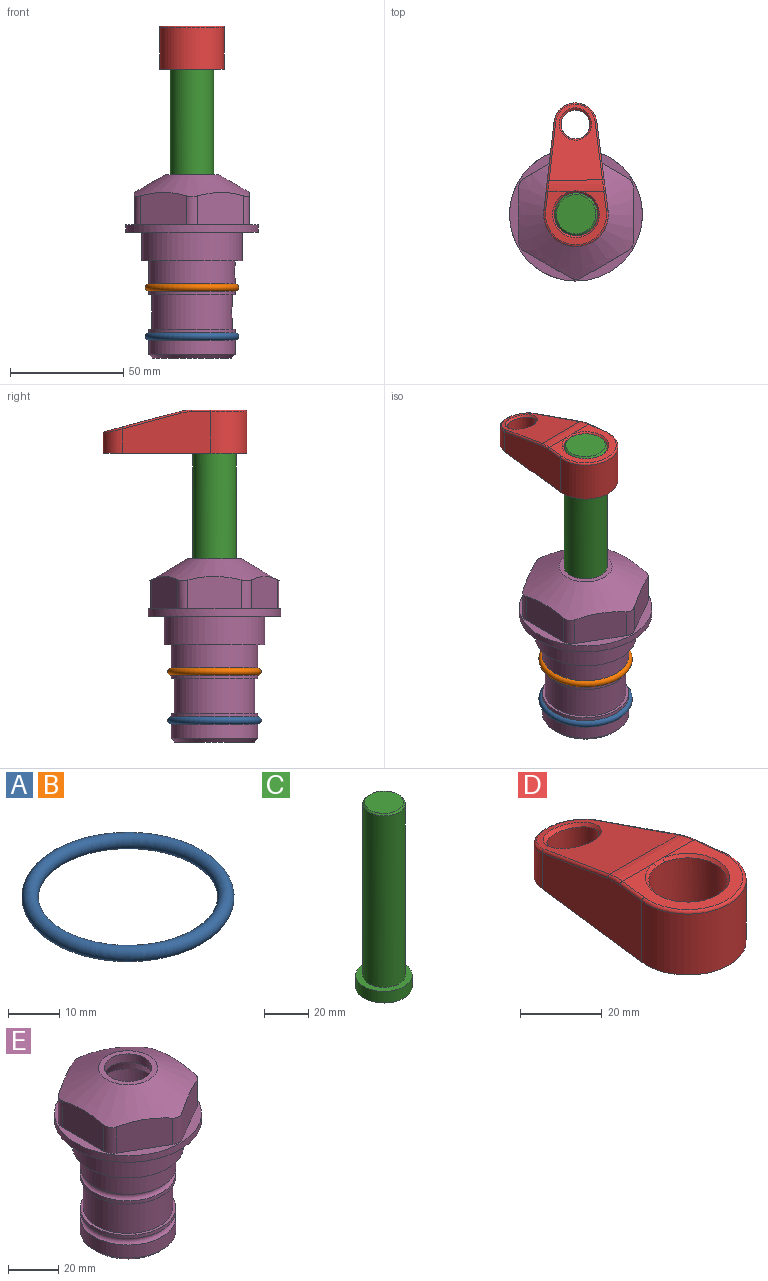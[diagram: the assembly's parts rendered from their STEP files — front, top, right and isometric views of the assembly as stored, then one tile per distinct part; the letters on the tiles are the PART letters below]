
ASSEMBLY  parts=5 mates=4
PART A: 1 faces, bbox 44.7x44.7x3.2 mm
  f0: torus R=19.05mm, axis (0,0,1), area 1193.9mm2
PART B: same geometry as A
PART C: 6 faces, bbox 25.4x25.4x101.6 mm
  f0: plane 17.46x17.46mm, normal (0,0,1), area 239.5mm2, adj f5
  f1: plane 25.4x25.4mm, normal (0,0,-1), area 506.7mm2, adj f2
  f2: cylinder r=12.7mm len=25.4mm, axis (0,0,1), area 506.7mm2, adj f1,f3
  f3: plane 25.4x25.4mm, normal (0,0,1), area 221.7mm2, adj f2,f4
  f4: cylinder r=9.53mm len=94.46mm, axis (0,0,1), area 5653mm2, adj f3,f5
  f5: cone r=8.73mm half-angle=45deg, axis (0,0,-1), area 64.4mm2, adj f0,f4
PART D: 31 faces, bbox 31.7x65.5x19.8 mm
  f0: plane 39.12x18.26mm, normal (0.99,0.12,0), area 612.2mm2, adj f1,f4,f7,f11,f13,f15
  f1: cylinder r=9.53mm len=18.91mm, axis (0,0,-1), area 296.1mm2, adj f0,f2,f7,f17
  f2: plane 39.12x18.26mm, normal (-0.99,0.12,0), area 612.2mm2, adj f1,f4,f7,f12,f14,f16
  f3: cylinder r=6.35mm len=12.7mm, axis (0,0,-1), area 362.4mm2, adj f7,f18
  f4: cylinder r=14.29mm len=28.58mm, axis (0,0,-1), area 882.2mm2, adj f0,f2,f7,f10
  f5: cylinder r=9.53mm len=19.05mm, axis (0,0,-1), area 1092.6mm2, adj f7,f19,f20
  f6: plane 26.99x23.69mm, normal (0,0,1), area 216.2mm2, adj f9,f10,f11,f12,f19
  f7: plane 63.5x28.58mm, normal (0,0,-1), area 661.8mm2, adj f0,f1,f2,f3,f4,f5,f22,f23
  f8: plane 33.52x23.6mm, normal (0,0.26,0.97), area 486mm2, adj f9,f15,f16,f17,f18
  f9: cylinder r=19.05mm len=24.72mm, axis (1,0,0), area 120.4mm2, adj f6,f8,f13,f14,f20
  f10: torus R=13.49mm, axis (0,0,1), area 59mm2, adj f4,f6,f11,f12
  f11: cylinder r=0.79mm len=8.67mm, axis (0.12,-0.99,0), area 10.8mm2, adj f0,f6,f10,f13
  f12: cylinder r=0.79mm len=8.67mm, axis (0.12,0.99,0), area 10.8mm2, adj f2,f6,f10,f14
  f13: bspline ~4.95x1.42mm, area 6.1mm2, adj f0,f9,f11,f15
  f14: bspline ~4.95x1.42mm, area 6.1mm2, adj f2,f9,f12,f16
  f15: cylinder r=0.79mm len=25.95mm, axis (0.12,-0.96,0.26), area 32.9mm2, adj f0,f8,f13,f17
  f16: cylinder r=0.79mm len=25.95mm, axis (0.12,0.96,-0.26), area 32.9mm2, adj f2,f8,f14,f17
  f17: bspline ~18.91x8.38mm, area 30mm2, adj f1,f8,f15,f16
  f18: bspline ~14.29x14.29mm, area 48.3mm2, adj f3,f8
  f19: cone r=9.53mm half-angle=45deg, axis (0,0,1), area 66.5mm2, adj f5,f6,f20
  f20: bspline ~3.22x0.96mm, area 3.5mm2, adj f5,f9,f19
  f21: plane 2.75x2.72mm, normal (0,0,-1), area 2.9mm2, adj f23,f25,f28
  f22: plane 23.05x15.88mm, normal (-0.99,-0.12,0), area 323.6mm2, adj f7,f25,f26,f27,f28,f29
  f23: plane 23.05x15.88mm, normal (0.99,-0.12,0), area 323.6mm2, adj f7,f21,f25,f27,f28,f30
  f24: cylinder r=9.53mm len=10.69mm, axis (0,0,-1), area 114.7mm2, adj f7,f27,f29,f30
  f25: cylinder r=12.7mm len=20.59mm, axis (0,0,-1), area 381.1mm2, adj f7,f21,f22,f23,f26,f28
  f26: plane 2.75x2.72mm, normal (0,0,-1), area 2.9mm2, adj f22,f25,f28
  f27: plane 19.72x18.37mm, normal (0,-0.26,-0.97), area 291.8mm2, adj f22,f23,f24,f28,f29,f30
  f28: cylinder r=15.88mm len=19.92mm, axis (1,0,0), area 54.8mm2, adj f21,f22,f23,f25,f26,f27
  f29: cylinder r=1.59mm len=11mm, axis (0,0,-1), area 34.7mm2, adj f7,f22,f24,f27
  f30: cylinder r=1.59mm len=11mm, axis (0,0,-1), area 34.7mm2, adj f7,f23,f24,f27
PART E: 36 faces, bbox 58.7x58.7x81 mm
  f0: cylinder r=17.78mm len=35.56mm, axis (0,0,1), area 1670.8mm2, adj f23,f24,f31
  f1: cylinder r=19.05mm len=38.1mm, axis (0,0,1), area 1191.9mm2, adj f26,f27,f30
  f2: plane 58.66x58.66mm, normal (0,0,-1), area 1150.6mm2, adj f3,f28
  f3: cylinder r=29.33mm len=58.66mm, axis (0,0,-1), area 585.1mm2, adj f2,f4
  f4: plane 58.66x58.66mm, normal (0,0,1), area 475.9mm2, adj f3,f5,f6,f7,f8,f9,f10,f11
  f5: plane 20.32x14.34mm, normal (-0.5,0.87,0), area 324.4mm2, adj f4,f15,f16,f17
  f6: plane 20.32x14.34mm, normal (0.5,0.87,0), area 324.4mm2, adj f4,f14,f15,f17
  f7: plane 23.48x14.34mm, normal (1,0,0), area 324.4mm2, adj f4,f13,f14,f17
  f8: plane 20.32x14.34mm, normal (0.5,-0.87,0), area 324.4mm2, adj f4,f12,f13,f17
  f9: plane 20.32x14.34mm, normal (-0.5,-0.87,0), area 324.4mm2, adj f4,f11,f12,f17
  f10: plane 23.48x14.34mm, normal (-1,0,0), area 324.4mm2, adj f4,f11,f16,f17
  f11: cylinder r=5.08mm len=12.85mm, axis (0,0,-1), area 67.2mm2, adj f4,f9,f10,f17
  f12: cylinder r=5.08mm len=12.85mm, axis (0,0,-1), area 67.2mm2, adj f4,f8,f9,f17
  f13: cylinder r=5.08mm len=12.85mm, axis (0,0,-1), area 67.2mm2, adj f4,f7,f8,f17
  f14: cylinder r=5.08mm len=12.85mm, axis (0,0,-1), area 67.2mm2, adj f4,f6,f7,f17
  f15: cylinder r=5.08mm len=12.85mm, axis (0,0,-1), area 67.2mm2, adj f4,f5,f6,f17
  f16: cylinder r=5.08mm len=12.85mm, axis (0,0,-1), area 67.2mm2, adj f4,f5,f10,f17
  f17: cone r=11.73mm half-angle=60deg, axis (0,0,-1), area 2071.8mm2, adj f5,f6,f7,f8,f9,f10,f11,f12
  f18: plane 23.46x23.46mm, normal (0,0,1), area 147.4mm2, adj f17,f35
  f19: plane 34.93x34.93mm, normal (0,0,-1), area 958mm2, adj f29
  f20: cylinder r=19.05mm len=38.1mm, axis (0,0,1), area 760.1mm2, adj f21,f29
  f21: torus R=19.05mm, axis (0,0,1), area 565.3mm2, adj f20,f22
  f22: cylinder r=19.05mm len=38.1mm, axis (0,0,1), area 190mm2, adj f21,f23
  f23: plane 38.1x38.1mm, normal (0,0,1), area 146.9mm2, adj f0,f22
  f24: plane 38.1x38.1mm, normal (0,0,-1), area 146.9mm2, adj f0,f25
  f25: cylinder r=19.05mm len=38.1mm, axis (0,0,1), area 190mm2, adj f24,f26
  f26: torus R=19.05mm, axis (0,0,1), area 565.3mm2, adj f1,f25
  f27: plane 44.45x44.45mm, normal (0,0,-1), area 411.7mm2, adj f1,f28
  f28: cylinder r=22.23mm len=44.45mm, axis (0,0,1), area 1773.5mm2, adj f2,f27
  f29: cone r=19.05mm half-angle=45deg, axis (0,0,1), area 257.5mm2, adj f19,f20
  f30: cylinder r=3.17mm len=6.75mm, axis (-1,0,0), area 128mm2, adj f1,f33
  f31: cylinder r=3.17mm len=6.35mm, axis (-1,0,0), area 102.5mm2, adj f0,f33
  f32: plane 25.4x25.4mm, normal (0,0,1), area 506.7mm2, adj f33
  f33: cylinder r=12.7mm len=66.42mm, axis (0,0,-1), area 5236.2mm2, adj f30,f31,f32,f34
  f34: cone r=9.53mm half-angle=30deg, axis (0,0,-1), area 443.4mm2, adj f33,f35
  f35: cylinder r=9.53mm len=19.05mm, axis (0,0,-1), area 240.9mm2, adj f18,f34
PLACE A t=(0,0,-21.59)mm
PLACE B at identity
PLACE C rot(axis=(0,0,1),0.4deg) t=(0,0,27.55)mm
PLACE D rot(axis=(0,0,1),0.4deg) t=(0,0,27.55)mm
PLACE E at identity fixed
MATE fastened B.f0 <-> E.f0  axis (0,0,1) through (0,0,-24.51)mm
MATE fastened C.f2 <-> D.f4  axis (0,0,1) through (0,0,91.05)mm
MATE cylindrical E.f0 <-> C.f2  axis (0,0,1) through (0,0,-50.55)mm
MATE fastened A.f0 <-> E.f0  axis (0,0,1) through (0,0,-46.1)mm
